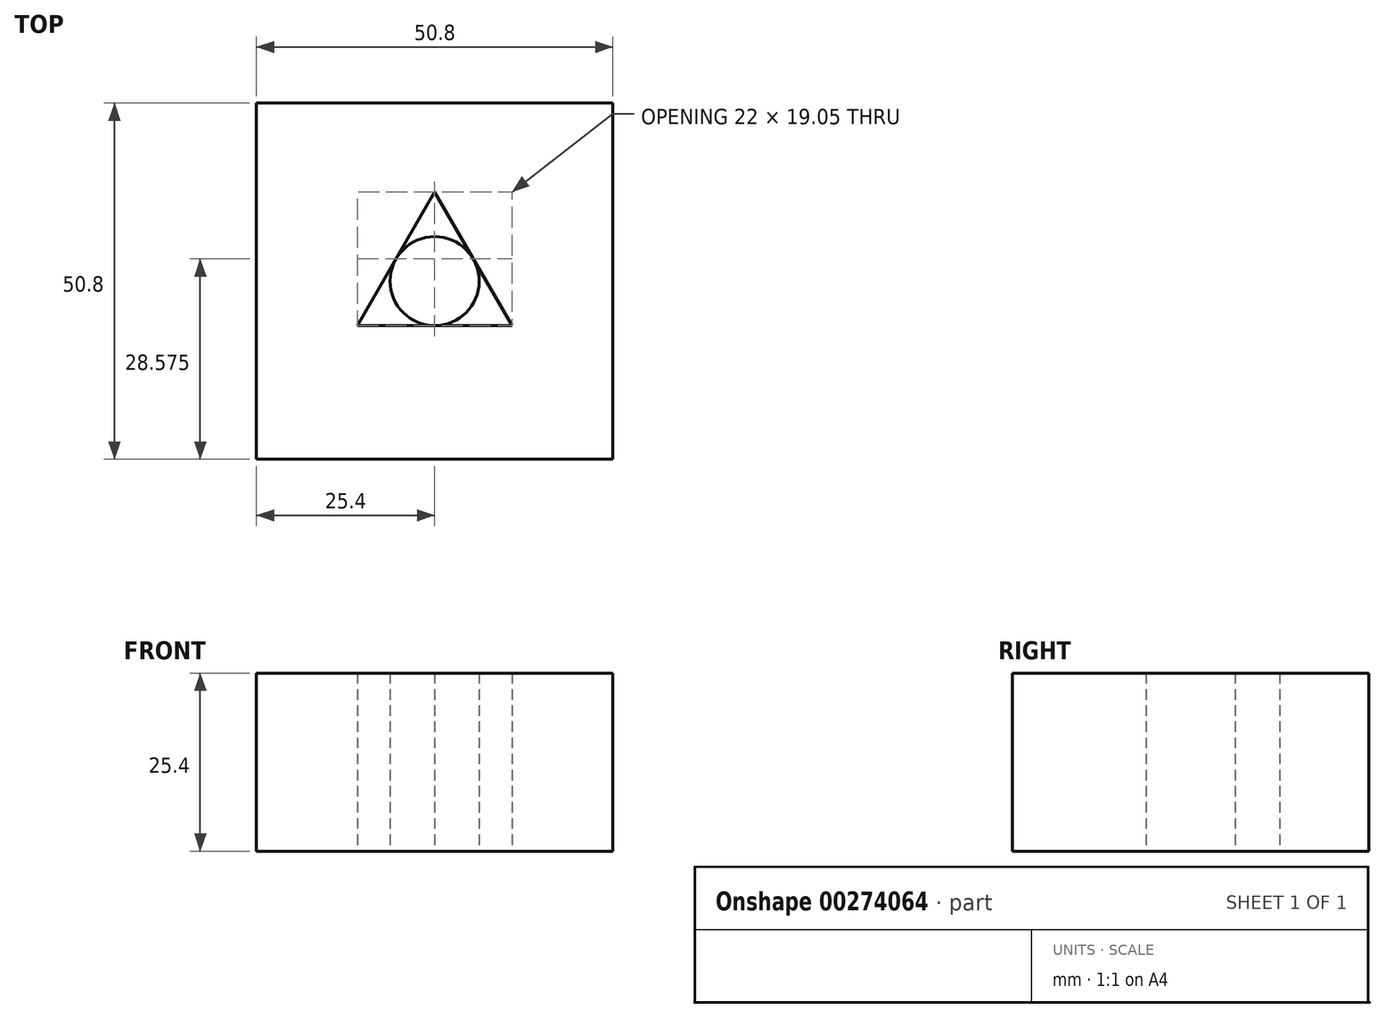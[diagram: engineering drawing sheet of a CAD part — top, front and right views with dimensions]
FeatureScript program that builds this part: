
annotation { "Feature Type Name" : "Feature", "Feature Type Description" : "" }
export const myFeature = defineFeature(function(context is Context, id is Id, definition is map)
    precondition{}
    {
        {
            var Q0;
            Q0=qCreatedBy(makeId("Top.planeOp"),FACE);
            var sketch = newSketch(context, id + "F0", { "sketchPlane" : qUnion([Q0])});
            skLineSegment(sketch, "E0.bottom", {"start": v(25.4, 25.4) * mm, "end": v(-25.4, 25.4) * mm});
            skLineSegment(sketch, "E0.top", {"start": v(25.4, -25.4) * mm, "end": v(-25.4, -25.4) * mm});
            skLineSegment(sketch, "E0.left", {"start": v(25.4, 25.4) * mm, "end": v(25.4, -25.4) * mm});
            skLineSegment(sketch, "E0.right", {"start": v(-25.4, 25.4) * mm, "end": v(-25.4, -25.4) * mm});
            skPoint(sketch, "E0.middle", {"position": v(0, 0) * mm});
            skCircle(sketch, "E1", {"center": v(0, 0) * mm, "radius": 6.35 * mm});
            skCircle(sketch, "E2.cCircle", {"center": v(0, 0) * mm, "radius": 6.35 * mm, "construction": true});
            skLineSegment(sketch, "E2.0", {"start": v(0, 12.7) * mm, "end": v(11, -6.35) * mm});
            skLineSegment(sketch, "E2.1", {"start": v(11, -6.35) * mm, "end": v(-11, -6.35) * mm});
            skLineSegment(sketch, "E2.2", {"start": v(-11, -6.35) * mm, "end": v(0, 12.7) * mm});
            skPoint(sketch, "E2.0.midPoint", {"position": v(5.5, 3.17) * mm});
            skSolve(sketch);
        }
        {
            var Q0;
            Q0=makeQuery(id+"F0.imprint","IMPRINT",FACE,{"disambiguationData":[TD([[makeQuery(id+"F0.imprint","IMPRINT",EDGE,{"derivedFrom":sQuery(id+"F0.wireOp",EDGE,"E0.bottom")}),1.0]])]});
            var Q1;
            {var subQ0=sQuery(id+"F0.wireOp",EDGE,"E1");var subQ1=makeQuery(id+"F0.imprint","INTERSECT",VERTEX,{"derivedFrom":[subQ0,sQuery(id+"F0.wireOp",EDGE,"E2.2")]});Q1=makeQuery(id+"F0.imprint","IMPRINT",FACE,{"disambiguationData":[TD([[makeQuery(id+"F0.imprint","IMPRINT",EDGE,{"disambiguationData":[TD([[subQ1,1.0]])],"derivedFrom":subQ0}),1.0]])]});}
            extrude(context, id + "F1", {"entities" : qUnion([Q0, Q1]), "depth" : 25.4 * mm});
        }
    });
